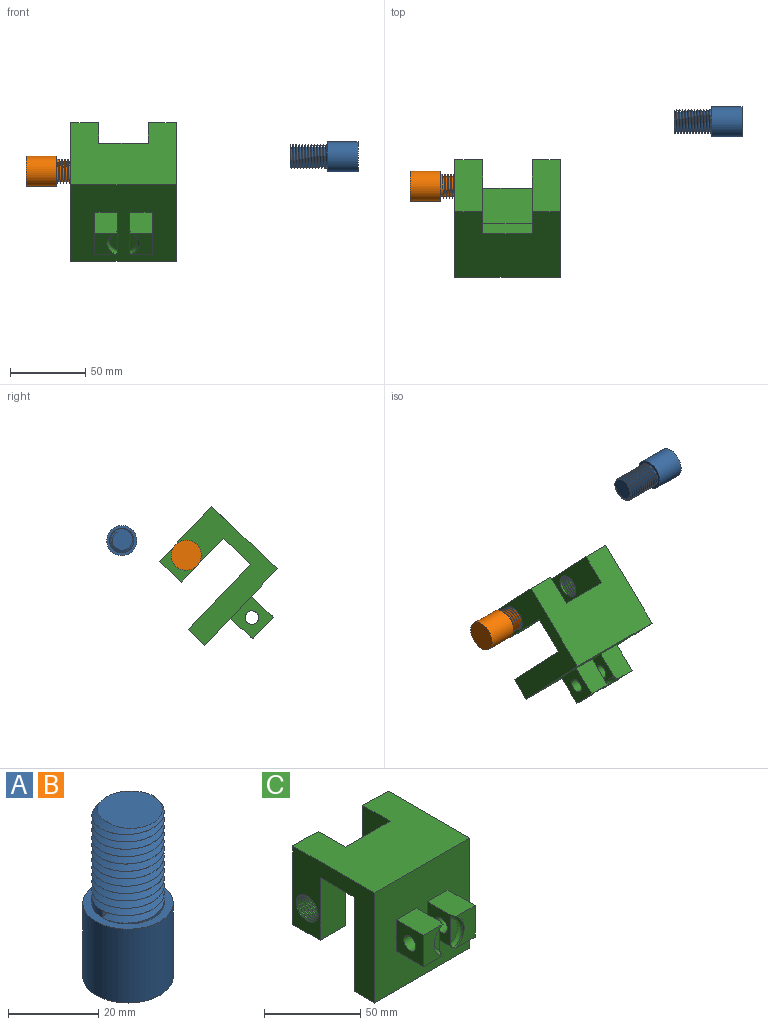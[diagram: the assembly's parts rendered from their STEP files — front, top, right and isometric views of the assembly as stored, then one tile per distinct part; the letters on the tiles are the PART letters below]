
ASSEMBLY  parts=3 mates=1
PART A: 8 faces, bbox 21.4x21.4x47.7 mm
  f0: cylinder r=8mm len=25mm, axis (0,0,-1), area 102.5mm2, adj f2,f4,f5,f6,f7
  f1: cylinder r=10mm len=20mm, axis (0,0,-1), area 1256.6mm2, adj f2,f3
  f2: plane 20x20mm, normal (0,0,1), area 113.1mm2, adj f0,f1
  f3: plane 20x20mm, normal (0,0,-1), area 314.2mm2, adj f1
  f4: plane 15.74x15.71mm, normal (0,0,1), area 161.1mm2, adj f0,f6,f7
  f5: plane 1.99x1.72mm, normal (0,-1,0), area 1.7mm2, adj f0,f6,f7
  f6: bspline ~26x18.48mm, area 1097.6mm2, adj f0,f4,f5,f7
  f7: bspline ~25.33x18.48mm, area 1046.9mm2, adj f0,f4,f5,f6
PART B: same geometry as A
PART C: 42 faces, bbox 72.5x81.4x70.8 mm
  f0: cylinder r=7.5mm len=18.5mm, axis (1,0,0), area 268.4mm2, adj f5,f24,f39,f40,f41
  f1: plane 20.2x18.27mm, normal (1,0,0), area 277.6mm2, adj f10,f13,f15,f22,f35,f37
  f2: plane 20.2x18.27mm, normal (-1,0,0), area 277.6mm2, adj f10,f17,f18,f21,f33,f38
  f3: plane 50x18.5mm, normal (0,1,0), area 925mm2, adj f4,f6,f12,f28
  f4: plane 70.81x60.81mm, normal (-1,0,0), area 2099mm2, adj f3,f7,f9,f10,f11,f12,f23,f26
  f5: plane 50x20mm, normal (-1,0,0), area 823.3mm2, adj f0,f8,f12,f29,f31,f32
  f6: plane 50x20mm, normal (1,0,0), area 823.3mm2, adj f3,f7,f12,f28,f30,f32
  f7: cylinder r=7.5mm len=18.5mm, axis (1,0,0), area 180.9mm2, adj f4,f6,f25,f26,f27
  f8: plane 50x18.5mm, normal (0,1,0), area 925mm2, adj f5,f12,f24,f29
  f9: plane 70x60mm, normal (0,1,0), area 4200mm2, adj f4,f11,f23,f24
  f10: plane 70x70mm, normal (0,-1,0), area 4300mm2, adj f1,f2,f4,f11,f12,f13,f14,f15
  f11: plane 70x15mm, normal (0,0,-1), area 1050mm2, adj f4,f9,f10,f24
  f12: plane 70x60mm, normal (0,0,1), area 3540mm2, adj f3,f4,f5,f6,f8,f10,f24,f32
  f13: plane 20.25x15.25mm, normal (0,0,1), area 299mm2, adj f1,f10,f14,f16,f36,f37
  f14: plane 20x20mm, normal (-1,0,0), area 336.4mm2, adj f10,f13,f15,f16,f22
  f15: plane 20.25x15.25mm, normal (0,0,-1), area 299mm2, adj f1,f10,f14,f16,f36,f37
  f16: plane 20x14.42mm, normal (0,-1,0), area 196.1mm2, adj f13,f14,f15,f36
  f17: plane 20.25x15.25mm, normal (0,0,1), area 299mm2, adj f2,f10,f19,f20,f34,f38
  f18: plane 20.25x15.25mm, normal (0,0,-1), area 299mm2, adj f2,f10,f19,f20,f34,f38
  f19: plane 20x20mm, normal (1,0,0), area 336.4mm2, adj f10,f17,f18,f20,f21
  f20: plane 20x14.42mm, normal (0,-1,0), area 196.1mm2, adj f17,f18,f19,f34
  f21: cylinder r=4.5mm len=15mm, axis (-1,0,0), area 424.1mm2, adj f2,f19
  f22: cylinder r=4.5mm len=15mm, axis (-1,0,0), area 424.1mm2, adj f1,f14
  f23: plane 70x25mm, normal (0,0,-1), area 1750mm2, adj f4,f9,f24,f30,f31,f32
  f24: plane 70.81x60.81mm, normal (1,0,0), area 2099mm2, adj f0,f8,f9,f10,f11,f12,f23,f29
  f25: plane 1.5x1.3mm, normal (0,1,0), area 1mm2, adj f7,f26,f27
  f26: bspline ~20.32x19.42mm, area 697.7mm2, adj f4,f7,f25,f27
  f27: bspline ~20.32x18.75mm, area 670.4mm2, adj f4,f7,f25,f26
  f28: plane 20x18.5mm, normal (0,0,-1), area 370mm2, adj f3,f4,f6,f30
  f29: plane 20x18.5mm, normal (0,0,-1), area 370mm2, adj f5,f8,f24,f31
  f30: plane 40x18.5mm, normal (0,-1,0), area 740mm2, adj f4,f6,f23,f28
  f31: plane 40x18.5mm, normal (0,-1,0), area 740mm2, adj f5,f23,f24,f29
  f32: plane 33x10mm, normal (0,1,0), area 330mm2, adj f5,f6,f12,f23
  f33: plane 16.12x5mm, normal (0,-1,0), area 57.7mm2, adj f2,f38
  f34: cylinder r=11mm len=20mm, axis (0,-1,0), area 25.1mm2, adj f17,f18,f20,f38
  f35: plane 16.12x5mm, normal (0,-1,0), area 57.7mm2, adj f1,f37
  f36: cylinder r=11mm len=20mm, axis (0,-1,0), area 25.1mm2, adj f13,f15,f16,f37
  f37: torus R=9mm, axis (0,-1,0), area 74.6mm2, adj f1,f13,f15,f35,f36
  f38: torus R=9mm, axis (0,-1,0), area 74.6mm2, adj f2,f17,f18,f33,f34
  f39: bspline ~20.32x19.42mm, area 697.7mm2, adj f0,f24,f40,f41
  f40: bspline ~20.32x18.75mm, area 670.4mm2, adj f0,f24,f39,f41
  f41: plane 1.5x1.3mm, normal (0,0,1), area 1mm2, adj f0,f39,f40
PLACE A rot(axis=(0,-1,0),90deg) t=(54.52,20.49,15.22)mm
PLACE B rot(axis=(0.35,0.87,0.35),97.9deg) t=(-165.44,-22.24,5.53)mm
PLACE C rot(axis=(1,0,0),43.5deg) t=(-100.82,-47.62,-18.56)mm
MATE cylindrical C.f0 <-> B.f0  axis (-1,0,0) through (-135.82,-22.24,5.53)mm
